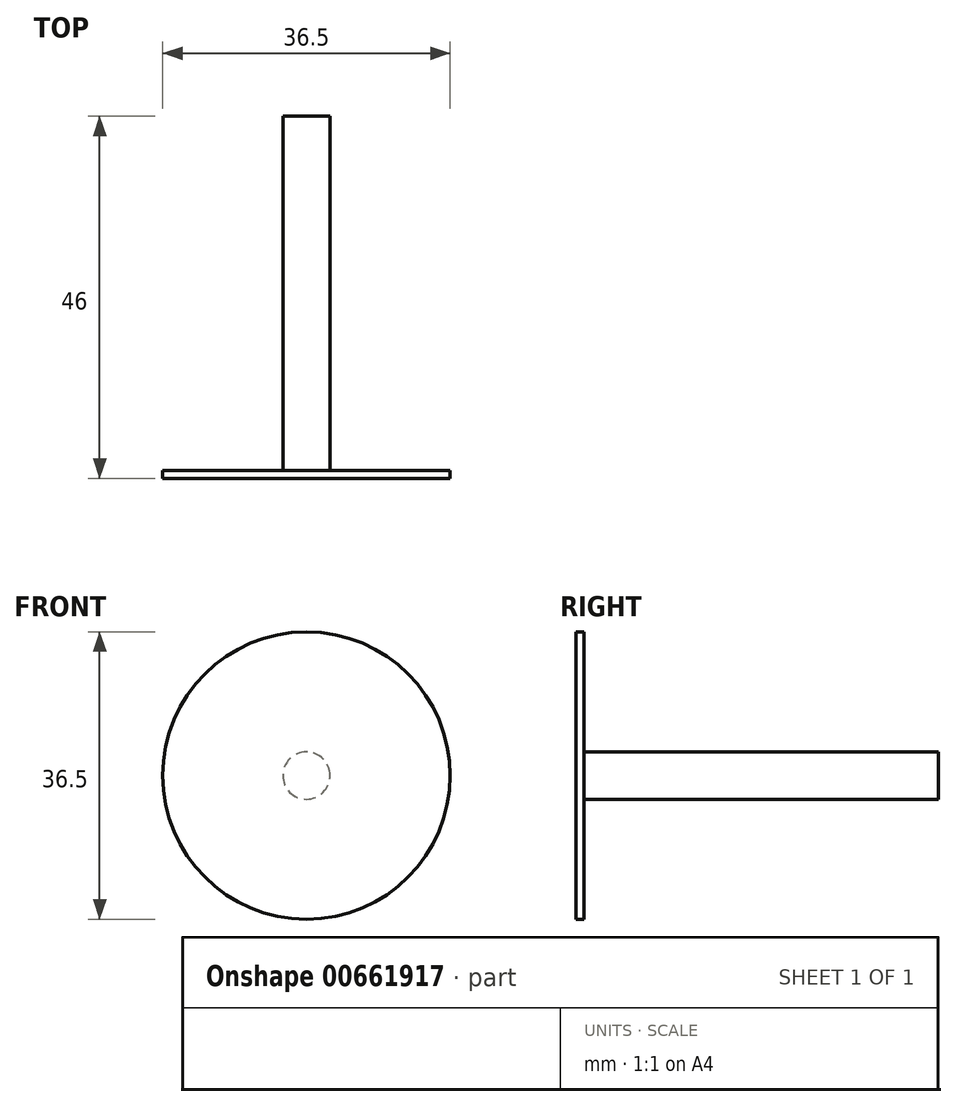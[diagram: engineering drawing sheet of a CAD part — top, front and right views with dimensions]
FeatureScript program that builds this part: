
annotation { "Feature Type Name" : "Feature", "Feature Type Description" : "" }
export const myFeature = defineFeature(function(context is Context, id is Id, definition is map)
    precondition{}
    {
        {
            var Q0;
            Q0=qCreatedBy(makeId("Front.planeOp"),FACE);
            var sketch = newSketch(context, id + "F0", { "sketchPlane" : qUnion([Q0])});
            skCircle(sketch, "E0", {"center": v(0, 0) * mm, "radius": 3 * mm});
            skSolve(sketch);
        }
        {
            var Q0;
            Q0 = qSketchRegion(id + "F0", true);
            extrude(context, id + "F1", {"entities" : qUnion([Q0]), "depth" : 45 * mm, "offsetDistance" : 25 * mm});
        }
        {
            var Q0;
            Q0=makeQuery(id+"F1.opExtrude","CAP_FACE",FACE,{"disambiguationData":[OSD([sQuery(id+"F0.wireOp",EDGE,"E0")])],"isStart":false});
            var sketch = newSketch(context, id + "F2", { "sketchPlane" : qUnion([Q0])});
            skCircle(sketch, "E1", {"center": v(0, 0) * mm, "radius": 18.25 * mm});
            skSolve(sketch);
        }
        {
            var Q0;
            Q0=makeQuery(id+"F2.imprint","IMPRINT",FACE,{"disambiguationData":[TD([[makeQuery(id+"F2.imprint","IMPRINT",EDGE,{"derivedFrom":sQuery(id+"F2.wireOp",EDGE,"E1")}),1.0]])]});
            var Q1;
            Q1=makeQuery(id+"F2.imprint","IMPRINT",FACE,{"disambiguationData":[TD([[makeQuery(id+"F2.imprint","IMPRINT",EDGE,{"derivedFrom":makeQuery(id+"F1.opExtrude","CAP_EDGE",EDGE,{"disambiguationData":[OSD([sQuery(id+"F0.wireOp",EDGE,"E0")])],"isStart":false})}),1.0]])]});
            extrude(context, id + "F3", {"entities" : qUnion([Q0, Q1]), "operationType" : NewBodyOperationType.ADD, "depth" : 1 * mm, "offsetDistance" : 25 * mm});
        }
    });
